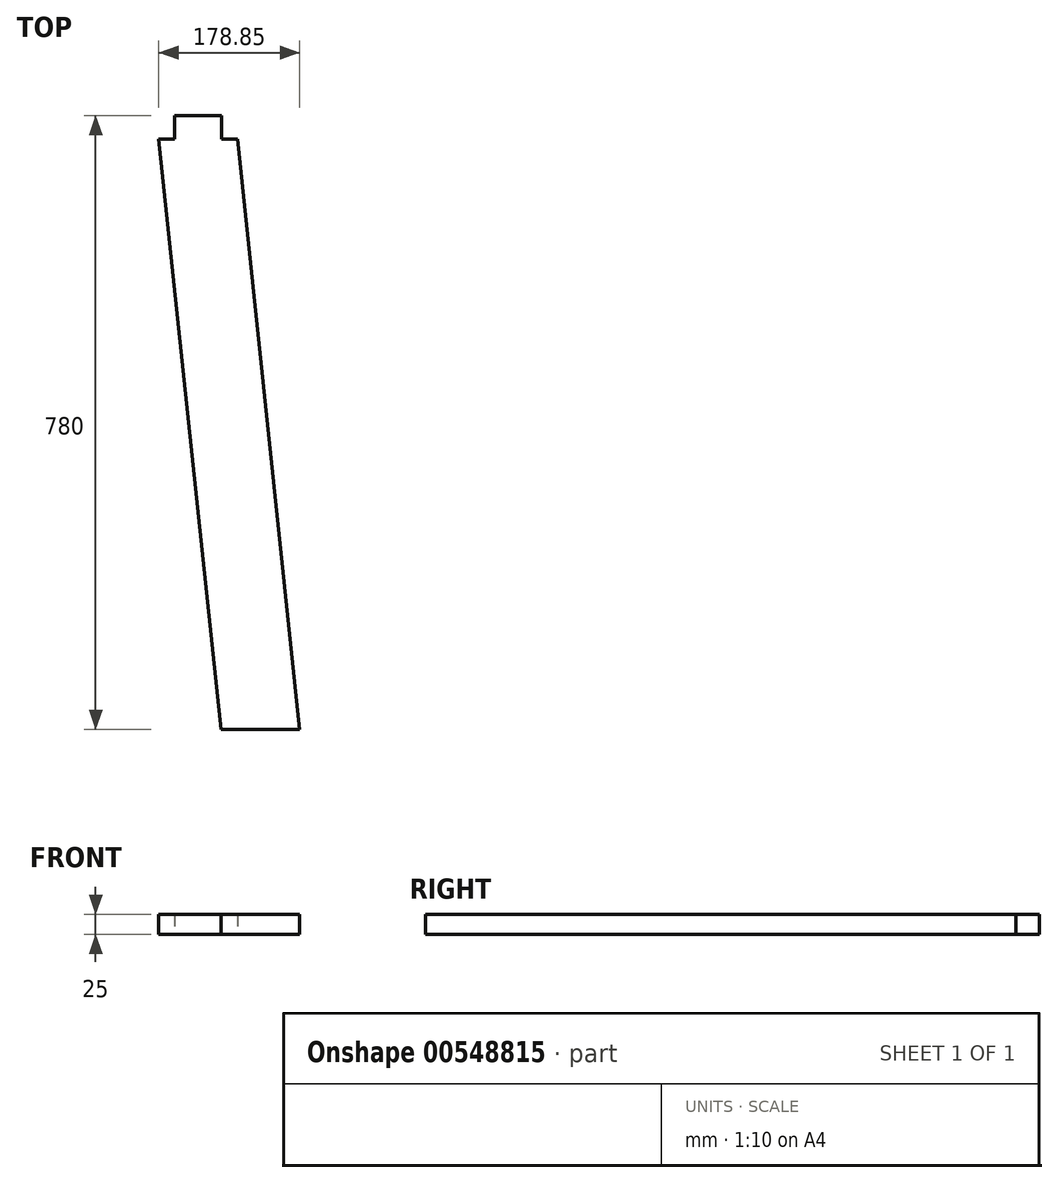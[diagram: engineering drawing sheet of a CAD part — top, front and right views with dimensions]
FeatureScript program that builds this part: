
annotation { "Feature Type Name" : "Feature", "Feature Type Description" : "" }
export const myFeature = defineFeature(function(context is Context, id is Id, definition is map)
    precondition{}
    {
        {
            var Q0;
            Q0=qCreatedBy(makeId("Top.planeOp"),FACE);
            var sketch = newSketch(context, id + "F0", { "sketchPlane" : qUnion([Q0])});
            skLineSegment(sketch, "E0.bottom", {"start": v(-254.6, 600.75) * mm, "end": v(-314.6, 600.75) * mm});
            skLineSegment(sketch, "E0.left", {"start": v(-254.6, 600.75) * mm, "end": v(-254.6, 570.75) * mm});
            skLineSegment(sketch, "E0.right", {"start": v(-314.6, 600.75) * mm, "end": v(-314.6, 570.75) * mm});
            skLineSegment(sketch, "E1", {"start": v(-314.6, 570.75) * mm, "end": v(-334.6, 570.75) * mm});
            skLineSegment(sketch, "E2", {"start": v(-254.6, 570.75) * mm, "end": v(-234.6, 570.75) * mm});
            skLineSegment(sketch, "E3", {"start": v(-334.6, 570.75) * mm, "end": v(-255.74, -179.25) * mm});
            skLineSegment(sketch, "E4", {"start": v(-155.74, -179.25) * mm, "end": v(-234.6, 570.75) * mm});
            skLineSegment(sketch, "E5", {"start": v(-255.74, -179.25) * mm, "end": v(-155.74, -179.25) * mm});
            skSolve(sketch);
        }
        {
            var Q0;
            Q0 = qSketchRegion(id + "F0", true);
            extrude(context, id + "F1", {"entities" : qUnion([Q0]), "depth" : 25 * mm, "offsetDistance" : 25 * mm});
        }
    });
